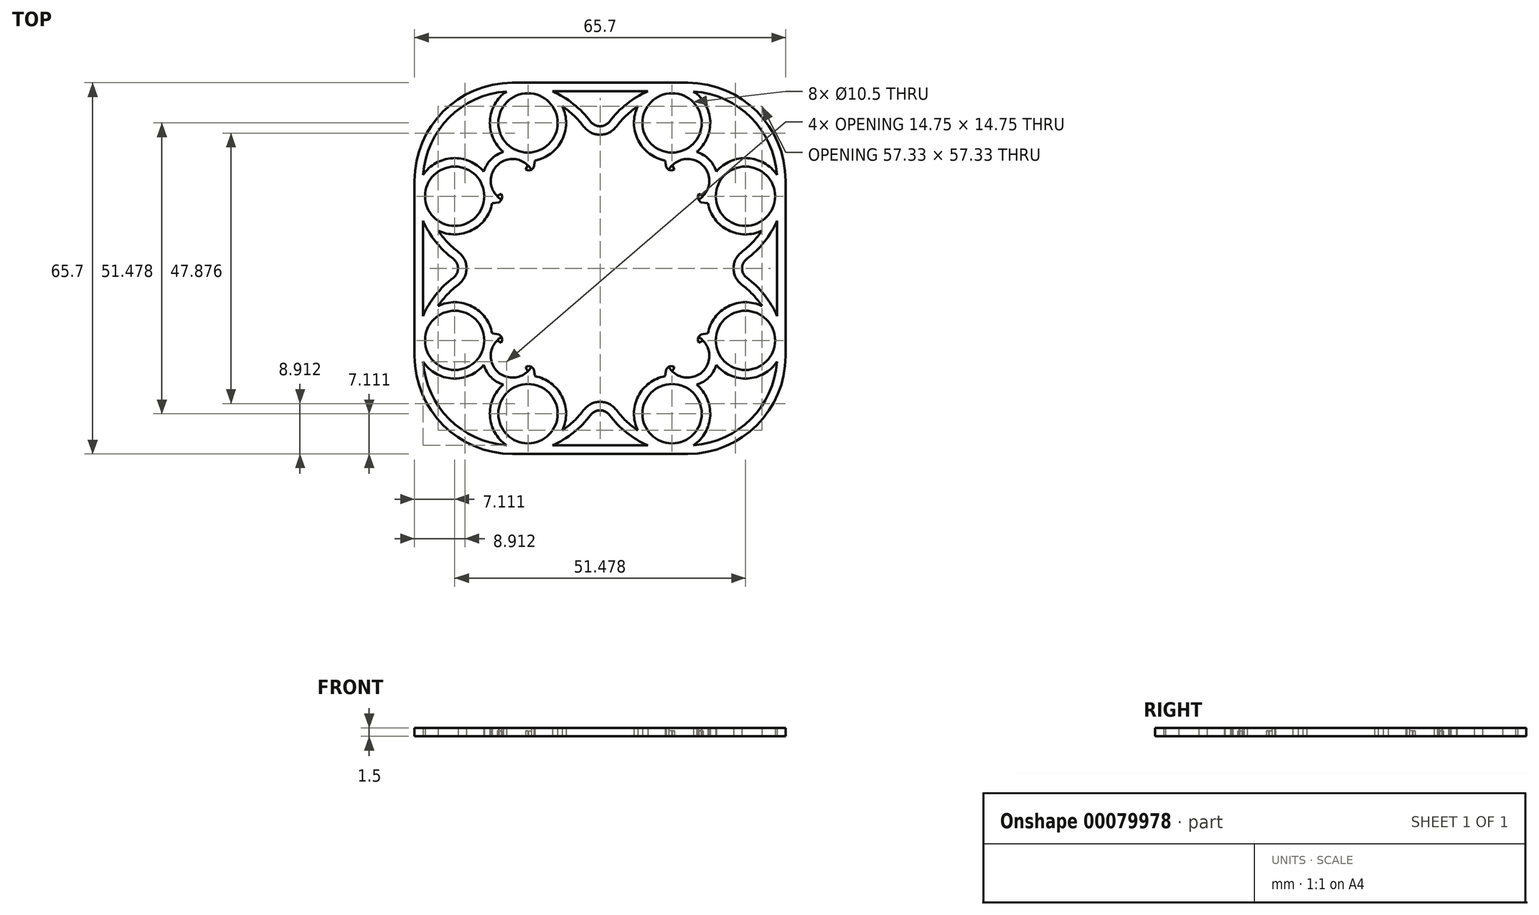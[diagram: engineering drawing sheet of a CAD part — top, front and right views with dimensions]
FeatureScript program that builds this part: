
annotation { "Feature Type Name" : "Feature", "Feature Type Description" : "" }
export const myFeature = defineFeature(function(context is Context, id is Id, definition is map)
    precondition{}
    {
        {
            var Q0;
            Q0=qCreatedBy(makeId("Top.planeOp"),FACE);
            var sketch = newSketch(context, id + "F0", { "sketchPlane" : qUnion([Q0])});
            skLineSegment(sketch, "E0.bottom", {"start": v(-15.5, 15.5) * mm, "end": v(15.5, 15.5) * mm});
            skLineSegment(sketch, "E0.top", {"start": v(-15.5, -15.5) * mm, "end": v(15.5, -15.5) * mm});
            skLineSegment(sketch, "E0.left", {"start": v(-15.5, 15.5) * mm, "end": v(-15.5, -15.5) * mm});
            skLineSegment(sketch, "E0.right", {"start": v(15.5, 15.5) * mm, "end": v(15.5, -15.5) * mm});
            skPoint(sketch, "E0.middle", {"position": v(0, 0) * mm});
            skCircle(sketch, "E1", {"center": v(-15.5, 15.5) * mm, "radius": 15 * mm});
            skCircle(sketch, "E2", {"center": v(15.5, 15.5) * mm, "radius": 15 * mm});
            skCircle(sketch, "E3", {"center": v(-15.5, -15.5) * mm, "radius": 15 * mm});
            skCircle(sketch, "E4", {"center": v(15.5, -15.5) * mm, "radius": 15 * mm});
            skLineSegment(sketch, "E5.bottom", {"start": v(-10, 10) * mm, "end": v(10, 10) * mm});
            skLineSegment(sketch, "E5.top", {"start": v(-10, -10) * mm, "end": v(10, -10) * mm});
            skLineSegment(sketch, "E5.left", {"start": v(-10, 10) * mm, "end": v(-10, -10) * mm});
            skLineSegment(sketch, "E5.right", {"start": v(10, 10) * mm, "end": v(10, -10) * mm});
            skCircle(sketch, "E6", {"center": v(-15.5, 15.5) * mm, "radius": 4.5 * mm});
            skCircle(sketch, "E7", {"center": v(-15.5, 15.5) * mm, "radius": 3.5 * mm});
            skCircle(sketch, "E8", {"center": v(15.5, 15.5) * mm, "radius": 3.5 * mm});
            skCircle(sketch, "E9", {"center": v(15.5, 15.5) * mm, "radius": 4.5 * mm});
            skCircle(sketch, "E10", {"center": v(15.5, -15.5) * mm, "radius": 4.5 * mm});
            skCircle(sketch, "E11", {"center": v(15.5, -15.5) * mm, "radius": 3.5 * mm});
            skCircle(sketch, "E12", {"center": v(-15.5, -15.5) * mm, "radius": 3.5 * mm});
            skCircle(sketch, "E13", {"center": v(-15.5, -15.5) * mm, "radius": 4.5 * mm});
            skLineSegment(sketch, "E14", {"start": v(-15.5, 15.5) * mm, "end": v(-18.68, 12.32) * mm});
            skLineSegment(sketch, "E15", {"start": v(-18.68, 12.32) * mm, "end": v(-12.32, 18.68) * mm});
            skLineSegment(sketch, "E16", {"start": v(-17.9, 11.7) * mm, "end": v(-11.7, 17.9) * mm});
            skLineSegment(sketch, "E17", {"start": v(-13.24, 16.34) * mm, "end": v(-13.95, 17.05) * mm});
            skSolve(sketch);
        }
        {
            var Q0;
            Q0=qCreatedBy(makeId("Top.planeOp"),FACE);
            var sketch = newSketch(context, id + "F1", { "sketchPlane" : qUnion([Q0])});
            skPoint(sketch, "E18.0", {"position": v(-15.5, 15.5) * mm});
            skArc(sketch, "E19", {"start": v(-2.86, 25.06) * mm, "mid": v(-4.62, 27.02) * mm, "end": v(-6.67, 28.67) * mm});
            skArc(sketch, "E20", {"start": v(-12.78, 18.22) * mm, "mid": v(-18.22, 18.22) * mm, "end": v(-18.22, 12.78) * mm});
            skLineSegment(sketch, "E21", {"start": v(-15.5, 32.85) * mm, "end": v(0, 32.85) * mm});
            skLineSegment(sketch, "E22", {"start": v(-8.44, 31.35) * mm, "end": v(0, 31.35) * mm});
            skLineSegment(sketch, "E23", {"start": v(-32.85, 15.5) * mm, "end": v(-32.85, 0) * mm});
            skLineSegment(sketch, "E24", {"start": v(-31.35, 8.44) * mm, "end": v(-31.35, 0) * mm});
            skArc(sketch, "E25.trimOffspring", {"start": v(-15.5, 32.85) * mm, "mid": v(-27.77, 27.77) * mm, "end": v(-32.85, 15.5) * mm});
            skPoint(sketch, "E26.orphan", {"position": v(-15.5, 31.35) * mm});
            skArc(sketch, "E27.trimOffspring", {"start": v(-31.35, 8.44) * mm, "mid": v(-29.09, 4.71) * mm, "end": v(-25.97, 1.66) * mm});
            skPoint(sketch, "E28.orphan", {"position": v(-31.35, 15.5) * mm});
            skArc(sketch, "E29", {"start": v(-25.14, 0) * mm, "mid": v(-25.36, 0.93) * mm, "end": v(-25.97, 1.66) * mm});
            skArc(sketch, "E30", {"start": v(-23.64, 0) * mm, "mid": v(-24.02, 1.6) * mm, "end": v(-25.06, 2.86) * mm});
            skLineSegment(sketch, "E31.0", {"start": v(-18.68, 12.32) * mm, "end": v(-18.22, 12.78) * mm});
            skLineSegment(sketch, "E32.0", {"start": v(-17.9, 11.7) * mm, "end": v(-17.42, 12.16) * mm});
            skLineSegment(sketch, "E33", {"start": v(-18.22, 12.78) * mm, "end": v(-17.47, 13.15) * mm});
            skLineSegment(sketch, "E34", {"start": v(-17.47, 13.15) * mm, "end": v(-17.3, 12.68) * mm});
            skLineSegment(sketch, "E35", {"start": v(-17.3, 12.68) * mm, "end": v(-17.42, 12.16) * mm});
            skLineSegment(sketch, "E36", {"start": v(-20.67, 14.12) * mm, "end": v(-30.8, 11.4) * mm});
            skLineSegment(sketch, "E37", {"start": v(-14.12, 20.67) * mm, "end": v(-11.4, 30.8) * mm});
            skPoint(sketch, "E38.0", {"position": v(-10, 10) * mm});
            skLineSegment(sketch, "E39.MirrorCS", {"start": v(-12.78, 18.22) * mm, "end": v(-13.15, 17.47) * mm});
            skLineSegment(sketch, "E40.MirrorCS", {"start": v(-12.68, 17.3) * mm, "end": v(-12.16, 17.42) * mm});
            skLineSegment(sketch, "E41.MirrorCS", {"start": v(-13.15, 17.47) * mm, "end": v(-12.68, 17.3) * mm});
            skLineSegment(sketch, "E42", {"start": v(-17.9, 11.7) * mm, "end": v(-19.1, 11.54) * mm});
            skLineSegment(sketch, "E43", {"start": v(-11.7, 17.9) * mm, "end": v(-11.54, 19.1) * mm});
            skArc(sketch, "E44.trimOffspring", {"start": v(-17.13, 20.6) * mm, "mid": v(-19.28, 19.28) * mm, "end": v(-20.6, 17.13) * mm});
            skArc(sketch, "E45.trimOffspring", {"start": v(-16.56, 31.31) * mm, "mid": v(-26.7, 26.7) * mm, "end": v(-31.31, 16.56) * mm});
            skArc(sketch, "E46.trimOffspring", {"start": v(-28.67, 6.67) * mm, "mid": v(-27.02, 4.62) * mm, "end": v(-25.06, 2.86) * mm});
            skLineSegment(sketch, "E47.trimOffspring", {"start": v(-12.78, 18.22) * mm, "end": v(-12.32, 18.68) * mm});
            skLineSegment(sketch, "E48.trimOffspring", {"start": v(-12.16, 17.42) * mm, "end": v(-11.7, 17.9) * mm});
            skArc(sketch, "E49.3.0", {"start": v(-1.66, 25.97) * mm, "mid": v(-0.93, 25.36) * mm, "end": v(0, 25.14) * mm});
            skArc(sketch, "E49.3.18", {"start": v(-2.86, 25.06) * mm, "mid": v(-1.6, 24.02) * mm, "end": v(0, 23.64) * mm});
            skArc(sketch, "E50.trimOffspring", {"start": v(-1.66, 25.97) * mm, "mid": v(-4.71, 29.09) * mm, "end": v(-8.44, 31.35) * mm});
            skPoint(sketch, "E51.orphan", {"position": v(-3.59, 27.23) * mm});
            skPoint(sketch, "E52.orphan", {"position": v(-2.09, 27.23) * mm});
            skPoint(sketch, "E53.orphan", {"position": v(-18.81, 0) * mm});
            skCircle(sketch, "E54", {"center": v(-25.74, 12.76) * mm, "radius": 5.25 * mm});
            skCircle(sketch, "E55", {"center": v(-12.76, 25.74) * mm, "radius": 5.25 * mm});
            skArc(sketch, "E56", {"start": v(-16.56, 31.31) * mm, "mid": v(-19.5, 26.1) * mm, "end": v(-17.13, 20.6) * mm});
            skArc(sketch, "E57", {"start": v(-28.67, 6.67) * mm, "mid": v(-22.68, 6.74) * mm, "end": v(-19.1, 11.54) * mm});
            skArc(sketch, "E58.trimOffspring", {"start": v(-20.6, 17.13) * mm, "mid": v(-26.1, 19.5) * mm, "end": v(-31.31, 16.56) * mm});
            skArc(sketch, "E59.trimOffspring", {"start": v(-11.54, 19.1) * mm, "mid": v(-6.74, 22.68) * mm, "end": v(-6.67, 28.67) * mm});
            skArc(sketch, "E60.1.0", {"start": v(-17.13, -20.6) * mm, "mid": v(-19.5, -26.1) * mm, "end": v(-16.56, -31.31) * mm});
            skArc(sketch, "E60.1.1", {"start": v(-6.67, -28.67) * mm, "mid": v(-6.74, -22.68) * mm, "end": v(-11.54, -19.1) * mm});
            skArc(sketch, "E60.1.2", {"start": v(-20.6, -17.13) * mm, "mid": v(-19.28, -19.28) * mm, "end": v(-17.13, -20.6) * mm});
            skArc(sketch, "E60.1.3", {"start": v(-19.1, -11.54) * mm, "mid": v(-22.68, -6.74) * mm, "end": v(-28.67, -6.67) * mm});
            skPoint(sketch, "E60.1.4", {"position": v(-31.35, -15.5) * mm});
            skCircle(sketch, "E60.1.5", {"center": v(-12.76, -25.74) * mm, "radius": 5.25 * mm});
            skArc(sketch, "E60.1.6", {"start": v(-8.44, -31.35) * mm, "mid": v(-4.71, -29.09) * mm, "end": v(-1.66, -25.97) * mm});
            skPoint(sketch, "E60.1.7", {"position": v(-10, -10) * mm});
            skArc(sketch, "E60.1.8", {"start": v(-31.31, -16.56) * mm, "mid": v(-26.1, -19.5) * mm, "end": v(-20.6, -17.13) * mm});
            skArc(sketch, "E60.1.9", {"start": v(-6.67, -28.67) * mm, "mid": v(-4.62, -27.02) * mm, "end": v(-2.86, -25.06) * mm});
            skArc(sketch, "E60.1.10", {"start": v(-25.97, -1.66) * mm, "mid": v(-29.09, -4.71) * mm, "end": v(-31.35, -8.44) * mm});
            skArc(sketch, "E60.1.11", {"start": v(-18.22, -12.78) * mm, "mid": v(-18.22, -18.22) * mm, "end": v(-12.78, -18.22) * mm});
            skLineSegment(sketch, "E60.1.12", {"start": v(-14.12, -20.67) * mm, "end": v(-11.4, -30.8) * mm});
            skPoint(sketch, "E60.1.13", {"position": v(0, -18.81) * mm});
            skPoint(sketch, "E60.1.14", {"position": v(-27.23, -2.09) * mm});
            skLineSegment(sketch, "E60.1.15", {"start": v(-32.85, -15.5) * mm, "end": v(-32.85, 0) * mm});
            skPoint(sketch, "E60.1.16", {"position": v(-15.5, -31.35) * mm});
            skPoint(sketch, "E60.1.17", {"position": v(-27.23, -3.59) * mm});
            skCircle(sketch, "E60.1.18", {"center": v(-25.74, -12.76) * mm, "radius": 5.25 * mm});
            skPoint(sketch, "E60.1.19", {"position": v(-15.5, -15.5) * mm});
            skLineSegment(sketch, "E60.1.20", {"start": v(-20.67, -14.12) * mm, "end": v(-30.8, -11.4) * mm});
            skArc(sketch, "E60.1.21", {"start": v(-32.85, -15.5) * mm, "mid": v(-27.77, -27.77) * mm, "end": v(-15.5, -32.85) * mm});
            skLineSegment(sketch, "E60.1.22", {"start": v(-8.44, -31.35) * mm, "end": v(0, -31.35) * mm});
            skLineSegment(sketch, "E60.1.23", {"start": v(-15.5, -32.85) * mm, "end": v(0, -32.85) * mm});
            skArc(sketch, "E60.1.24", {"start": v(-31.31, -16.56) * mm, "mid": v(-26.7, -26.7) * mm, "end": v(-16.56, -31.31) * mm});
            skLineSegment(sketch, "E60.1.25", {"start": v(-31.35, -8.44) * mm, "end": v(-31.35, 0) * mm});
            skArc(sketch, "E60.1.26", {"start": v(0, -23.64) * mm, "mid": v(-1.6, -24.02) * mm, "end": v(-2.86, -25.06) * mm});
            skArc(sketch, "E60.1.27", {"start": v(-25.06, -2.86) * mm, "mid": v(-27.02, -4.62) * mm, "end": v(-28.67, -6.67) * mm});
            skArc(sketch, "E60.1.28", {"start": v(0, -25.14) * mm, "mid": v(-0.93, -25.36) * mm, "end": v(-1.66, -25.97) * mm});
            skArc(sketch, "E60.1.29", {"start": v(-25.06, -2.86) * mm, "mid": v(-24.02, -1.6) * mm, "end": v(-23.64, 0) * mm});
            skArc(sketch, "E60.1.30", {"start": v(-25.97, -1.66) * mm, "mid": v(-25.36, -0.93) * mm, "end": v(-25.14, 0) * mm});
            skLineSegment(sketch, "E60.1.31", {"start": v(-18.22, -12.78) * mm, "end": v(-18.68, -12.32) * mm});
            skLineSegment(sketch, "E60.1.32", {"start": v(-17.3, -12.68) * mm, "end": v(-17.42, -12.16) * mm});
            skLineSegment(sketch, "E60.1.33", {"start": v(-12.78, -18.22) * mm, "end": v(-13.15, -17.47) * mm});
            skLineSegment(sketch, "E60.1.34", {"start": v(-18.22, -12.78) * mm, "end": v(-17.47, -13.15) * mm});
            skLineSegment(sketch, "E60.1.35", {"start": v(-17.9, -11.7) * mm, "end": v(-19.1, -11.54) * mm});
            skLineSegment(sketch, "E60.1.36", {"start": v(-17.42, -12.16) * mm, "end": v(-17.9, -11.7) * mm});
            skLineSegment(sketch, "E60.1.37", {"start": v(-11.7, -17.9) * mm, "end": v(-12.16, -17.42) * mm});
            skLineSegment(sketch, "E60.1.38", {"start": v(-12.32, -18.68) * mm, "end": v(-12.78, -18.22) * mm});
            skLineSegment(sketch, "E60.1.39", {"start": v(-11.7, -17.9) * mm, "end": v(-11.54, -19.1) * mm});
            skLineSegment(sketch, "E60.1.40", {"start": v(-13.15, -17.47) * mm, "end": v(-12.68, -17.3) * mm});
            skLineSegment(sketch, "E60.1.41", {"start": v(-17.47, -13.15) * mm, "end": v(-17.3, -12.68) * mm});
            skLineSegment(sketch, "E60.1.42", {"start": v(-12.68, -17.3) * mm, "end": v(-12.16, -17.42) * mm});
            skLineSegment(sketch, "E60.1.43", {"start": v(-17.42, -12.16) * mm, "end": v(-17.9, -11.7) * mm});
            skLineSegment(sketch, "E60.1.44", {"start": v(-11.7, -17.9) * mm, "end": v(-12.16, -17.42) * mm});
            skArc(sketch, "E60.2.0", {"start": v(20.6, -17.13) * mm, "mid": v(26.1, -19.5) * mm, "end": v(31.31, -16.56) * mm});
            skArc(sketch, "E60.2.1", {"start": v(28.67, -6.67) * mm, "mid": v(22.68, -6.74) * mm, "end": v(19.1, -11.54) * mm});
            skArc(sketch, "E60.2.2", {"start": v(17.13, -20.6) * mm, "mid": v(19.28, -19.28) * mm, "end": v(20.6, -17.13) * mm});
            skArc(sketch, "E60.2.3", {"start": v(11.54, -19.1) * mm, "mid": v(6.74, -22.68) * mm, "end": v(6.67, -28.67) * mm});
            skPoint(sketch, "E60.2.4", {"position": v(15.5, -31.35) * mm});
            skCircle(sketch, "E60.2.5", {"center": v(25.74, -12.76) * mm, "radius": 5.25 * mm});
            skArc(sketch, "E60.2.6", {"start": v(31.35, -8.44) * mm, "mid": v(29.09, -4.71) * mm, "end": v(25.97, -1.66) * mm});
            skPoint(sketch, "E60.2.7", {"position": v(10, -10) * mm});
            skArc(sketch, "E60.2.8", {"start": v(16.56, -31.31) * mm, "mid": v(19.5, -26.1) * mm, "end": v(17.13, -20.6) * mm});
            skArc(sketch, "E60.2.9", {"start": v(28.67, -6.67) * mm, "mid": v(27.02, -4.62) * mm, "end": v(25.06, -2.86) * mm});
            skArc(sketch, "E60.2.10", {"start": v(1.66, -25.97) * mm, "mid": v(4.71, -29.09) * mm, "end": v(8.44, -31.35) * mm});
            skArc(sketch, "E60.2.11", {"start": v(12.78, -18.22) * mm, "mid": v(18.22, -18.22) * mm, "end": v(18.22, -12.78) * mm});
            skLineSegment(sketch, "E60.2.12", {"start": v(20.67, -14.12) * mm, "end": v(30.8, -11.4) * mm});
            skPoint(sketch, "E60.2.13", {"position": v(18.81, 0) * mm});
            skPoint(sketch, "E60.2.14", {"position": v(2.09, -27.23) * mm});
            skLineSegment(sketch, "E60.2.15", {"start": v(15.5, -32.85) * mm, "end": v(0, -32.85) * mm});
            skPoint(sketch, "E60.2.16", {"position": v(31.35, -15.5) * mm});
            skPoint(sketch, "E60.2.17", {"position": v(3.59, -27.23) * mm});
            skCircle(sketch, "E60.2.18", {"center": v(12.76, -25.74) * mm, "radius": 5.25 * mm});
            skPoint(sketch, "E60.2.19", {"position": v(15.5, -15.5) * mm});
            skLineSegment(sketch, "E60.2.20", {"start": v(14.12, -20.67) * mm, "end": v(11.4, -30.8) * mm});
            skArc(sketch, "E60.2.21", {"start": v(15.5, -32.85) * mm, "mid": v(27.77, -27.77) * mm, "end": v(32.85, -15.5) * mm});
            skLineSegment(sketch, "E60.2.22", {"start": v(31.35, -8.44) * mm, "end": v(31.35, 0) * mm});
            skLineSegment(sketch, "E60.2.23", {"start": v(32.85, -15.5) * mm, "end": v(32.85, 0) * mm});
            skArc(sketch, "E60.2.24", {"start": v(16.56, -31.31) * mm, "mid": v(26.7, -26.7) * mm, "end": v(31.31, -16.56) * mm});
            skLineSegment(sketch, "E60.2.25", {"start": v(8.44, -31.35) * mm, "end": v(0, -31.35) * mm});
            skArc(sketch, "E60.2.26", {"start": v(23.64, 0) * mm, "mid": v(24.02, -1.6) * mm, "end": v(25.06, -2.86) * mm});
            skArc(sketch, "E60.2.27", {"start": v(2.86, -25.06) * mm, "mid": v(4.62, -27.02) * mm, "end": v(6.67, -28.67) * mm});
            skArc(sketch, "E60.2.28", {"start": v(25.14, 0) * mm, "mid": v(25.36, -0.93) * mm, "end": v(25.97, -1.66) * mm});
            skArc(sketch, "E60.2.29", {"start": v(2.86, -25.06) * mm, "mid": v(1.6, -24.02) * mm, "end": v(0, -23.64) * mm});
            skArc(sketch, "E60.2.30", {"start": v(1.66, -25.97) * mm, "mid": v(0.93, -25.36) * mm, "end": v(0, -25.14) * mm});
            skLineSegment(sketch, "E60.2.31", {"start": v(12.78, -18.22) * mm, "end": v(12.32, -18.68) * mm});
            skLineSegment(sketch, "E60.2.32", {"start": v(12.68, -17.3) * mm, "end": v(12.16, -17.42) * mm});
            skLineSegment(sketch, "E60.2.33", {"start": v(18.22, -12.78) * mm, "end": v(17.47, -13.15) * mm});
            skLineSegment(sketch, "E60.2.34", {"start": v(12.78, -18.22) * mm, "end": v(13.15, -17.47) * mm});
            skLineSegment(sketch, "E60.2.35", {"start": v(11.7, -17.9) * mm, "end": v(11.54, -19.1) * mm});
            skLineSegment(sketch, "E60.2.36", {"start": v(12.16, -17.42) * mm, "end": v(11.7, -17.9) * mm});
            skLineSegment(sketch, "E60.2.37", {"start": v(17.9, -11.7) * mm, "end": v(17.42, -12.16) * mm});
            skLineSegment(sketch, "E60.2.38", {"start": v(18.68, -12.32) * mm, "end": v(18.22, -12.78) * mm});
            skLineSegment(sketch, "E60.2.39", {"start": v(17.9, -11.7) * mm, "end": v(19.1, -11.54) * mm});
            skLineSegment(sketch, "E60.2.40", {"start": v(17.47, -13.15) * mm, "end": v(17.3, -12.68) * mm});
            skLineSegment(sketch, "E60.2.41", {"start": v(13.15, -17.47) * mm, "end": v(12.68, -17.3) * mm});
            skLineSegment(sketch, "E60.2.42", {"start": v(17.3, -12.68) * mm, "end": v(17.42, -12.16) * mm});
            skLineSegment(sketch, "E60.2.43", {"start": v(12.16, -17.42) * mm, "end": v(11.7, -17.9) * mm});
            skLineSegment(sketch, "E60.2.44", {"start": v(17.9, -11.7) * mm, "end": v(17.42, -12.16) * mm});
            skArc(sketch, "E60.3.0", {"start": v(17.13, 20.6) * mm, "mid": v(19.5, 26.1) * mm, "end": v(16.56, 31.31) * mm});
            skArc(sketch, "E60.3.1", {"start": v(6.67, 28.67) * mm, "mid": v(6.74, 22.68) * mm, "end": v(11.54, 19.1) * mm});
            skArc(sketch, "E60.3.2", {"start": v(20.6, 17.13) * mm, "mid": v(19.28, 19.28) * mm, "end": v(17.13, 20.6) * mm});
            skArc(sketch, "E60.3.3", {"start": v(19.1, 11.54) * mm, "mid": v(22.68, 6.74) * mm, "end": v(28.67, 6.67) * mm});
            skPoint(sketch, "E60.3.4", {"position": v(31.35, 15.5) * mm});
            skCircle(sketch, "E60.3.5", {"center": v(12.76, 25.74) * mm, "radius": 5.25 * mm});
            skArc(sketch, "E60.3.6", {"start": v(8.44, 31.35) * mm, "mid": v(4.71, 29.09) * mm, "end": v(1.66, 25.97) * mm});
            skPoint(sketch, "E60.3.7", {"position": v(10, 10) * mm});
            skArc(sketch, "E60.3.8", {"start": v(31.31, 16.56) * mm, "mid": v(26.1, 19.5) * mm, "end": v(20.6, 17.13) * mm});
            skArc(sketch, "E60.3.9", {"start": v(6.67, 28.67) * mm, "mid": v(4.62, 27.02) * mm, "end": v(2.86, 25.06) * mm});
            skArc(sketch, "E60.3.10", {"start": v(25.97, 1.66) * mm, "mid": v(29.09, 4.71) * mm, "end": v(31.35, 8.44) * mm});
            skArc(sketch, "E60.3.11", {"start": v(18.22, 12.78) * mm, "mid": v(18.22, 18.22) * mm, "end": v(12.78, 18.22) * mm});
            skLineSegment(sketch, "E60.3.12", {"start": v(14.12, 20.67) * mm, "end": v(11.4, 30.8) * mm});
            skPoint(sketch, "E60.3.13", {"position": v(0, 18.81) * mm});
            skPoint(sketch, "E60.3.14", {"position": v(27.23, 2.09) * mm});
            skLineSegment(sketch, "E60.3.15", {"start": v(32.85, 15.5) * mm, "end": v(32.85, 0) * mm});
            skPoint(sketch, "E60.3.16", {"position": v(15.5, 31.35) * mm});
            skPoint(sketch, "E60.3.17", {"position": v(27.23, 3.59) * mm});
            skCircle(sketch, "E60.3.18", {"center": v(25.74, 12.76) * mm, "radius": 5.25 * mm});
            skPoint(sketch, "E60.3.19", {"position": v(15.5, 15.5) * mm});
            skLineSegment(sketch, "E60.3.20", {"start": v(20.67, 14.12) * mm, "end": v(30.8, 11.4) * mm});
            skArc(sketch, "E60.3.21", {"start": v(32.85, 15.5) * mm, "mid": v(27.77, 27.77) * mm, "end": v(15.5, 32.85) * mm});
            skLineSegment(sketch, "E60.3.22", {"start": v(8.44, 31.35) * mm, "end": v(0, 31.35) * mm});
            skLineSegment(sketch, "E60.3.23", {"start": v(15.5, 32.85) * mm, "end": v(0, 32.85) * mm});
            skArc(sketch, "E60.3.24", {"start": v(31.31, 16.56) * mm, "mid": v(26.7, 26.7) * mm, "end": v(16.56, 31.31) * mm});
            skLineSegment(sketch, "E60.3.25", {"start": v(31.35, 8.44) * mm, "end": v(31.35, 0) * mm});
            skArc(sketch, "E60.3.26", {"start": v(0, 23.64) * mm, "mid": v(1.6, 24.02) * mm, "end": v(2.86, 25.06) * mm});
            skArc(sketch, "E60.3.27", {"start": v(25.06, 2.86) * mm, "mid": v(27.02, 4.62) * mm, "end": v(28.67, 6.67) * mm});
            skArc(sketch, "E60.3.28", {"start": v(0, 25.14) * mm, "mid": v(0.93, 25.36) * mm, "end": v(1.66, 25.97) * mm});
            skArc(sketch, "E60.3.29", {"start": v(25.06, 2.86) * mm, "mid": v(24.02, 1.6) * mm, "end": v(23.64, 0) * mm});
            skArc(sketch, "E60.3.30", {"start": v(25.97, 1.66) * mm, "mid": v(25.36, 0.93) * mm, "end": v(25.14, 0) * mm});
            skLineSegment(sketch, "E60.3.31", {"start": v(18.22, 12.78) * mm, "end": v(18.68, 12.32) * mm});
            skLineSegment(sketch, "E60.3.32", {"start": v(17.3, 12.68) * mm, "end": v(17.42, 12.16) * mm});
            skLineSegment(sketch, "E60.3.33", {"start": v(12.78, 18.22) * mm, "end": v(13.15, 17.47) * mm});
            skLineSegment(sketch, "E60.3.34", {"start": v(18.22, 12.78) * mm, "end": v(17.47, 13.15) * mm});
            skLineSegment(sketch, "E60.3.35", {"start": v(17.9, 11.7) * mm, "end": v(19.1, 11.54) * mm});
            skLineSegment(sketch, "E60.3.36", {"start": v(17.42, 12.16) * mm, "end": v(17.9, 11.7) * mm});
            skLineSegment(sketch, "E60.3.37", {"start": v(11.7, 17.9) * mm, "end": v(12.16, 17.42) * mm});
            skLineSegment(sketch, "E60.3.38", {"start": v(12.32, 18.68) * mm, "end": v(12.78, 18.22) * mm});
            skLineSegment(sketch, "E60.3.39", {"start": v(11.7, 17.9) * mm, "end": v(11.54, 19.1) * mm});
            skLineSegment(sketch, "E60.3.40", {"start": v(13.15, 17.47) * mm, "end": v(12.68, 17.3) * mm});
            skLineSegment(sketch, "E60.3.41", {"start": v(17.47, 13.15) * mm, "end": v(17.3, 12.68) * mm});
            skLineSegment(sketch, "E60.3.42", {"start": v(12.68, 17.3) * mm, "end": v(12.16, 17.42) * mm});
            skLineSegment(sketch, "E60.3.43", {"start": v(17.42, 12.16) * mm, "end": v(17.9, 11.7) * mm});
            skLineSegment(sketch, "E60.3.44", {"start": v(11.7, 17.9) * mm, "end": v(12.16, 17.42) * mm});
            skPoint(sketch, "E60.center", {"position": v(0, 0) * mm});
            skSolve(sketch);
        }
        {
            var Q0;
            Q0 = qSketchRegion(id + "F1", true);
            extrude(context, id + "F2", {"entities" : qUnion([Q0]), "depth" : 1.5 * mm});
        }
        {
            var Q0;
            Q0=makeQuery(id+"F2.opExtrude","CAP_FACE",FACE,{"disambiguationData":[OSD([sQuery(id+"F1.wireOp",EDGE,"E19"),sQuery(id+"F1.wireOp",EDGE,"E20"),sQuery(id+"F1.wireOp",EDGE,"E21"),sQuery(id+"F1.wireOp",EDGE,"E22"),sQuery(id+"F1.wireOp",EDGE,"E23"),sQuery(id+"F1.wireOp",EDGE,"E24"),sQuery(id+"F1.wireOp",EDGE,"E25.trimOffspring"),sQuery(id+"F1.wireOp",EDGE,"E27.trimOffspring"),sQuery(id+"F1.wireOp",EDGE,"E29"),sQuery(id+"F1.wireOp",EDGE,"E30"),sQuery(id+"F1.wireOp",EDGE,"E33"),sQuery(id+"F1.wireOp",EDGE,"E34"),sQuery(id+"F1.wireOp",EDGE,"E35"),sQuery(id+"F1.wireOp",EDGE,"E32.0"),sQuery(id+"F1.wireOp",EDGE,"E39.MirrorCS"),sQuery(id+"F1.wireOp",EDGE,"E40.MirrorCS"),sQuery(id+"F1.wireOp",EDGE,"E41.MirrorCS"),sQuery(id+"F1.wireOp",EDGE,"E42"),sQuery(id+"F1.wireOp",EDGE,"E43"),sQuery(id+"F1.wireOp",EDGE,"E44.trimOffspring"),sQuery(id+"F1.wireOp",EDGE,"E45.trimOffspring"),sQuery(id+"F1.wireOp",EDGE,"E46.trimOffspring"),sQuery(id+"F1.wireOp",EDGE,"E48.trimOffspring"),sQuery(id+"F1.wireOp",EDGE,"E49.3.0"),sQuery(id+"F1.wireOp",EDGE,"E49.3.18"),sQuery(id+"F1.wireOp",EDGE,"E50.trimOffspring"),sQuery(id+"F1.wireOp",EDGE,"E54"),sQuery(id+"F1.wireOp",EDGE,"E55"),sQuery(id+"F1.wireOp",EDGE,"E56"),sQuery(id+"F1.wireOp",EDGE,"E57"),sQuery(id+"F1.wireOp",EDGE,"E58.trimOffspring"),sQuery(id+"F1.wireOp",EDGE,"E59.trimOffspring"),sQuery(id+"F1.wireOp",EDGE,"E60.1.0"),sQuery(id+"F1.wireOp",EDGE,"E60.1.1"),sQuery(id+"F1.wireOp",EDGE,"E60.1.2"),sQuery(id+"F1.wireOp",EDGE,"E60.1.3"),sQuery(id+"F1.wireOp",EDGE,"E60.1.5"),sQuery(id+"F1.wireOp",EDGE,"E60.1.6"),sQuery(id+"F1.wireOp",EDGE,"E60.1.8"),sQuery(id+"F1.wireOp",EDGE,"E60.1.9"),sQuery(id+"F1.wireOp",EDGE,"E60.1.10"),sQuery(id+"F1.wireOp",EDGE,"E60.1.11"),sQuery(id+"F1.wireOp",EDGE,"E60.1.15"),sQuery(id+"F1.wireOp",EDGE,"E60.1.18"),sQuery(id+"F1.wireOp",EDGE,"E60.1.21"),sQuery(id+"F1.wireOp",EDGE,"E60.1.22"),sQuery(id+"F1.wireOp",EDGE,"E60.1.23"),sQuery(id+"F1.wireOp",EDGE,"E60.1.24"),sQuery(id+"F1.wireOp",EDGE,"E60.1.25"),sQuery(id+"F1.wireOp",EDGE,"E60.1.26"),sQuery(id+"F1.wireOp",EDGE,"E60.1.27"),sQuery(id+"F1.wireOp",EDGE,"E60.1.28"),sQuery(id+"F1.wireOp",EDGE,"E60.1.29"),sQuery(id+"F1.wireOp",EDGE,"E60.1.30"),sQuery(id+"F1.wireOp",EDGE,"E60.1.32"),sQuery(id+"F1.wireOp",EDGE,"E60.1.33"),sQuery(id+"F1.wireOp",EDGE,"E60.1.34"),sQuery(id+"F1.wireOp",EDGE,"E60.1.35"),sQuery(id+"F1.wireOp",EDGE,"E60.1.39"),sQuery(id+"F1.wireOp",EDGE,"E60.1.40"),sQuery(id+"F1.wireOp",EDGE,"E60.1.41"),sQuery(id+"F1.wireOp",EDGE,"E60.1.42"),sQuery(id+"F1.wireOp",EDGE,"E60.1.43"),sQuery(id+"F1.wireOp",EDGE,"E60.1.44"),sQuery(id+"F1.wireOp",EDGE,"E60.2.0"),sQuery(id+"F1.wireOp",EDGE,"E60.2.1"),sQuery(id+"F1.wireOp",EDGE,"E60.2.2"),sQuery(id+"F1.wireOp",EDGE,"E60.2.3"),sQuery(id+"F1.wireOp",EDGE,"E60.2.5"),sQuery(id+"F1.wireOp",EDGE,"E60.2.6"),sQuery(id+"F1.wireOp",EDGE,"E60.2.8"),sQuery(id+"F1.wireOp",EDGE,"E60.2.9"),sQuery(id+"F1.wireOp",EDGE,"E60.2.10"),sQuery(id+"F1.wireOp",EDGE,"E60.2.11"),sQuery(id+"F1.wireOp",EDGE,"E60.2.15"),sQuery(id+"F1.wireOp",EDGE,"E60.2.18"),sQuery(id+"F1.wireOp",EDGE,"E60.2.21"),sQuery(id+"F1.wireOp",EDGE,"E60.2.22"),sQuery(id+"F1.wireOp",EDGE,"E60.2.23"),sQuery(id+"F1.wireOp",EDGE,"E60.2.24"),sQuery(id+"F1.wireOp",EDGE,"E60.2.25"),sQuery(id+"F1.wireOp",EDGE,"E60.2.26"),sQuery(id+"F1.wireOp",EDGE,"E60.2.27"),sQuery(id+"F1.wireOp",EDGE,"E60.2.28"),sQuery(id+"F1.wireOp",EDGE,"E60.2.29"),sQuery(id+"F1.wireOp",EDGE,"E60.2.30"),sQuery(id+"F1.wireOp",EDGE,"E60.2.32"),sQuery(id+"F1.wireOp",EDGE,"E60.2.33"),sQuery(id+"F1.wireOp",EDGE,"E60.2.34"),sQuery(id+"F1.wireOp",EDGE,"E60.2.35"),sQuery(id+"F1.wireOp",EDGE,"E60.2.39"),sQuery(id+"F1.wireOp",EDGE,"E60.2.40"),sQuery(id+"F1.wireOp",EDGE,"E60.2.41"),sQuery(id+"F1.wireOp",EDGE,"E60.2.42"),sQuery(id+"F1.wireOp",EDGE,"E60.2.43"),sQuery(id+"F1.wireOp",EDGE,"E60.2.44"),sQuery(id+"F1.wireOp",EDGE,"E60.3.0"),sQuery(id+"F1.wireOp",EDGE,"E60.3.1"),sQuery(id+"F1.wireOp",EDGE,"E60.3.2"),sQuery(id+"F1.wireOp",EDGE,"E60.3.3"),sQuery(id+"F1.wireOp",EDGE,"E60.3.5"),sQuery(id+"F1.wireOp",EDGE,"E60.3.6"),sQuery(id+"F1.wireOp",EDGE,"E60.3.8"),sQuery(id+"F1.wireOp",EDGE,"E60.3.9"),sQuery(id+"F1.wireOp",EDGE,"E60.3.10"),sQuery(id+"F1.wireOp",EDGE,"E60.3.11"),sQuery(id+"F1.wireOp",EDGE,"E60.3.15"),sQuery(id+"F1.wireOp",EDGE,"E60.3.18"),sQuery(id+"F1.wireOp",EDGE,"E60.3.21"),sQuery(id+"F1.wireOp",EDGE,"E60.3.22"),sQuery(id+"F1.wireOp",EDGE,"E60.3.23"),sQuery(id+"F1.wireOp",EDGE,"E60.3.24"),sQuery(id+"F1.wireOp",EDGE,"E60.3.25"),sQuery(id+"F1.wireOp",EDGE,"E60.3.26"),sQuery(id+"F1.wireOp",EDGE,"E60.3.27"),sQuery(id+"F1.wireOp",EDGE,"E60.3.28"),sQuery(id+"F1.wireOp",EDGE,"E60.3.29"),sQuery(id+"F1.wireOp",EDGE,"E60.3.30"),sQuery(id+"F1.wireOp",EDGE,"E60.3.32"),sQuery(id+"F1.wireOp",EDGE,"E60.3.33"),sQuery(id+"F1.wireOp",EDGE,"E60.3.34"),sQuery(id+"F1.wireOp",EDGE,"E60.3.35"),sQuery(id+"F1.wireOp",EDGE,"E60.3.39"),sQuery(id+"F1.wireOp",EDGE,"E60.3.40"),sQuery(id+"F1.wireOp",EDGE,"E60.3.41"),sQuery(id+"F1.wireOp",EDGE,"E60.3.42"),sQuery(id+"F1.wireOp",EDGE,"E60.3.43"),sQuery(id+"F1.wireOp",EDGE,"E60.3.44")])],"isStart":false});
            var sketch = newSketch(context, id + "F3", { "sketchPlane" : qUnion([Q0])});
            skPoint(sketch, "E61.0", {"position": v(-15.5, 15.5) * mm});
            skPoint(sketch, "E62.0", {"position": v(-15.5, -15.5) * mm});
            skPoint(sketch, "E63.0", {"position": v(15.5, -15.5) * mm});
            skPoint(sketch, "E64.0", {"position": v(15.5, 15.5) * mm});
            skCircle(sketch, "E65", {"center": v(-15.5, 15.5) * mm, "radius": 3.85 * mm});
            skCircle(sketch, "E66", {"center": v(15.5, 15.5) * mm, "radius": 3.85 * mm});
            skCircle(sketch, "E67", {"center": v(15.5, -15.5) * mm, "radius": 3.85 * mm});
            skCircle(sketch, "E68", {"center": v(-15.5, -15.5) * mm, "radius": 3.85 * mm});
            skSolve(sketch);
        }
        {
            var Q0;
            Q0 = qSketchRegion(id + "F3", true);
            extrude(context, id + "F4", {"entities" : qUnion([Q0]), "operationType" : NewBodyOperationType.REMOVE, "oppositeDirection" : true, "depth" : 0.5 * mm});
        }
    });
